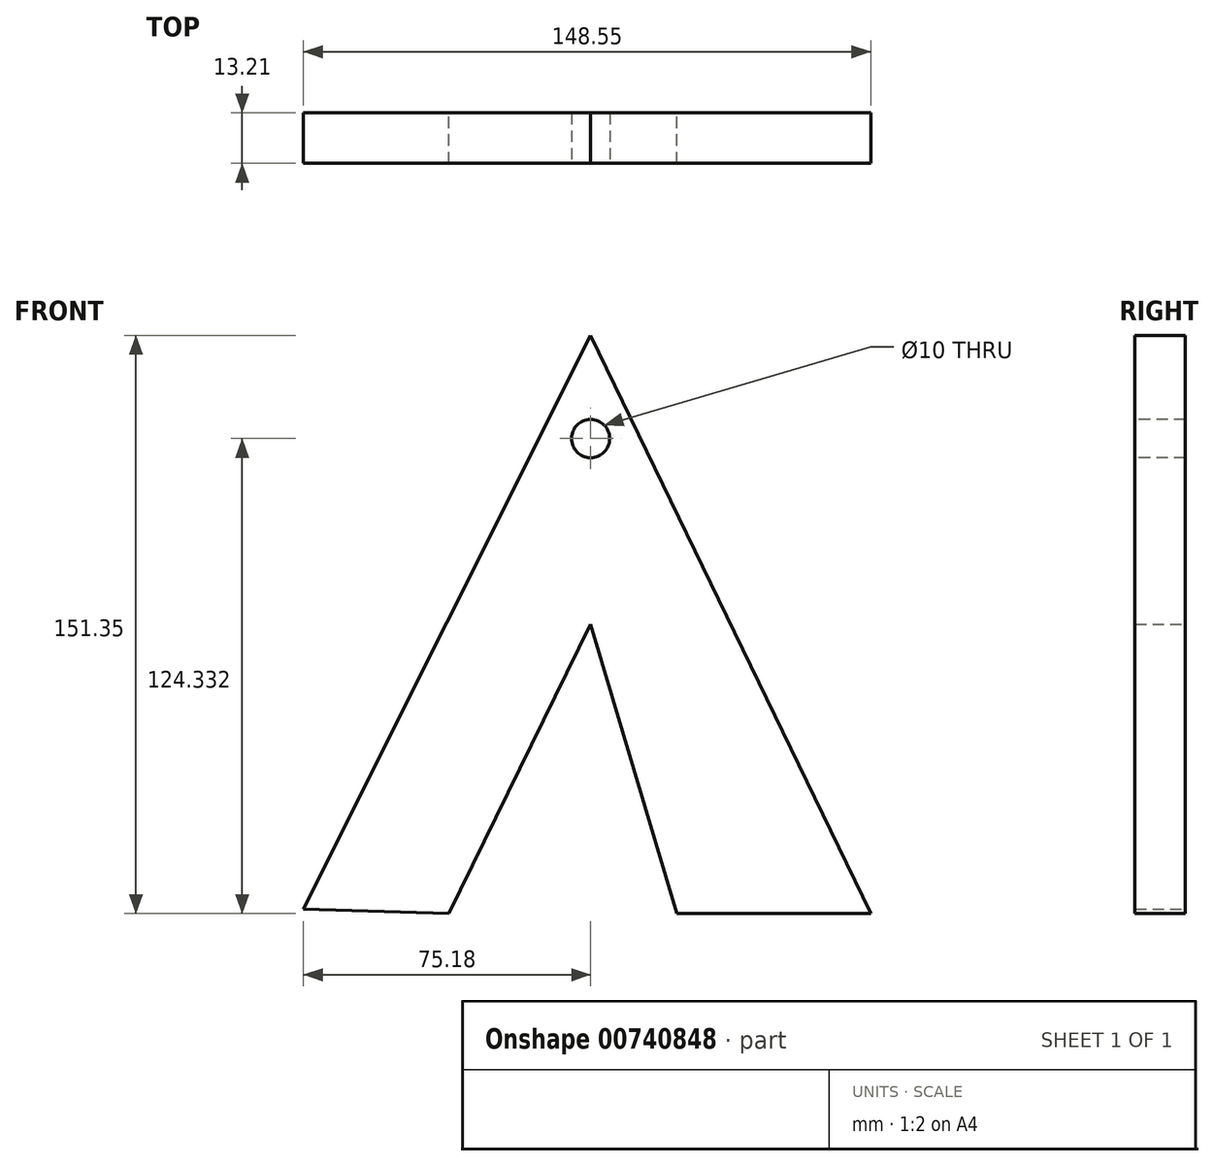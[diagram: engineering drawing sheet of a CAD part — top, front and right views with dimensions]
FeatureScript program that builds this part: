
annotation { "Feature Type Name" : "Feature", "Feature Type Description" : "" }
export const myFeature = defineFeature(function(context is Context, id is Id, definition is map)
    precondition{}
    {
        {
            var Q0;
            Q0=qCreatedBy(makeId("Front.planeOp"),FACE);
            var sketch = newSketch(context, id + "F0", { "sketchPlane" : qUnion([Q0])});
            skLineSegment(sketch, "E0", {"start": v(-75.18, -74.54) * mm, "end": v(0, 75.61) * mm});
            skLineSegment(sketch, "E1", {"start": v(0, 75.61) * mm, "end": v(73.37, -75.74) * mm});
            skLineSegment(sketch, "E2", {"start": v(73.37, -75.74) * mm, "end": v(22.64, -75.74) * mm});
            skLineSegment(sketch, "E3", {"start": v(22.64, -75.74) * mm, "end": v(0, 0) * mm});
            skLineSegment(sketch, "E4", {"start": v(0, 0) * mm, "end": v(-37.14, -75.74) * mm});
            skLineSegment(sketch, "E5", {"start": v(-37.14, -75.74) * mm, "end": v(-75.18, -74.54) * mm});
            skSolve(sketch);
        }
        {
            var Q0;
            Q0=makeQuery(id+"F0.imprint","IMPRINT",FACE,{"disambiguationData":[TD([[makeQuery(id+"F0.imprint","IMPRINT",EDGE,{"derivedFrom":sQuery(id+"F0.wireOp",EDGE,"E0")}),-1.0]])]});
            extrude(context, id + "F1", {"entities" : qUnion([Q0]), "depth" : 13.2 * mm, "offsetDistance" : 25.4 * mm});
        }
        {
            var Q0;
            Q0=makeQuery(id+"F1.opExtrude","CAP_FACE",FACE,{"disambiguationData":[OSD([sQuery(id+"F0.wireOp",EDGE,"E0"),sQuery(id+"F0.wireOp",EDGE,"E1"),sQuery(id+"F0.wireOp",EDGE,"E2"),sQuery(id+"F0.wireOp",EDGE,"E3"),sQuery(id+"F0.wireOp",EDGE,"E4"),sQuery(id+"F0.wireOp",EDGE,"E5")])],"isStart":false});
            var sketch = newSketch(context, id + "F2", { "sketchPlane" : qUnion([Q0])});
            skCircle(sketch, "E6", {"center": v(0, 48.6) * mm, "radius": 6.91 * mm});
            skSolve(sketch);
        }
        {
            var Q0;
            Q0=sQuery(id+"F2.wireOp",VERTEX,"E6.center");
            var Q1;
            Q1=makeQuery(id+"F1.opExtrude","SWEPT_BODY",BODY,{"disambiguationData":[OSD([sQuery(id+"F0.wireOp",EDGE,"E0"),sQuery(id+"F0.wireOp",EDGE,"E1"),sQuery(id+"F0.wireOp",EDGE,"E2"),sQuery(id+"F0.wireOp",EDGE,"E3"),sQuery(id+"F0.wireOp",EDGE,"E4"),sQuery(id+"F0.wireOp",EDGE,"E5")])]});
            hole(context, id + "F3", {"style" : HoleStyle.SIMPLE, "endStyle" : HoleEndStyle.THROUGH, "holeDiameter" : 10 * mm, "majorDiameter" : 6.35 * mm, "isTappedThrough" : true, "tappedDepth" : 12.7 * mm, "tapClearance" : 3, "locations" : qUnion([Q0]), "scope" : qUnion([Q1])});
        }
    });
